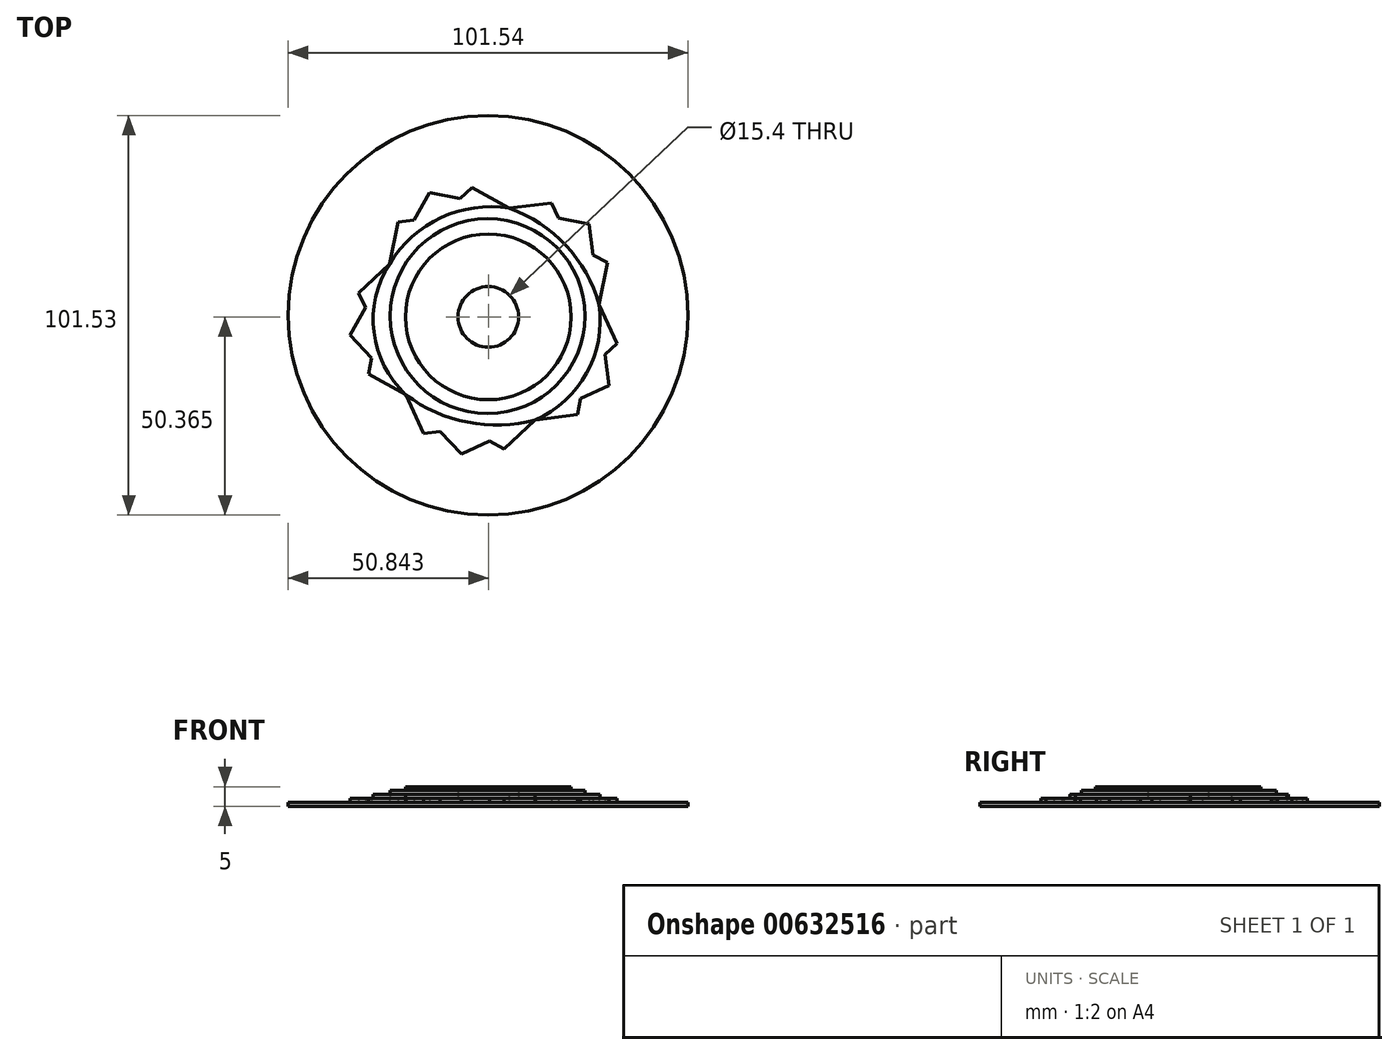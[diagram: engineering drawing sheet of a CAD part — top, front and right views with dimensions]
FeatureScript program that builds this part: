
annotation { "Feature Type Name" : "Feature", "Feature Type Description" : "" }
export const myFeature = defineFeature(function(context is Context, id is Id, definition is map)
    precondition{}
    {
        {
            var Q0;
            Q0=qCreatedBy(makeId("Top.planeOp"),FACE);
            var sketch = newSketch(context, id + "F0", { "sketchPlane" : qUnion([Q0])});
            skCircle(sketch, "E0.cCircle", {"center": v(-32.14, 16.2) * mm, "radius": 27.07 * mm, "construction": true});
            skLineSegment(sketch, "E0.0", {"start": v(0.71, 9.84) * mm, "end": v(-28.04, -17) * mm});
            skLineSegment(sketch, "E0.1", {"start": v(-28.04, -17) * mm, "end": v(-62.46, 2.05) * mm});
            skLineSegment(sketch, "E0.2", {"start": v(-62.46, 2.05) * mm, "end": v(-54.97, 40.67) * mm});
            skLineSegment(sketch, "E0.3", {"start": v(-54.97, 40.67) * mm, "end": v(-15.93, 45.48) * mm});
            skLineSegment(sketch, "E0.4", {"start": v(-15.93, 45.48) * mm, "end": v(0.71, 9.84) * mm});
            skPoint(sketch, "E0.0.midPoint", {"position": v(-13.66, -3.58) * mm});
            skLineSegment(sketch, "E1.0", {"start": v(-1.78, 30.3) * mm, "end": v(-9.36, -8.3) * mm});
            skLineSegment(sketch, "E1.1", {"start": v(-9.36, -8.3) * mm, "end": v(-48.4, -13.03) * mm});
            skLineSegment(sketch, "E1.2", {"start": v(-48.4, -13.03) * mm, "end": v(-64.97, 22.65) * mm});
            skLineSegment(sketch, "E1.3", {"start": v(-64.97, 22.65) * mm, "end": v(-36.16, 49.43) * mm});
            skLineSegment(sketch, "E1.4", {"start": v(-36.16, 49.43) * mm, "end": v(-1.78, 30.3) * mm});
            skPoint(sketch, "E1.0.midPoint", {"position": v(-5.57, 11) * mm});
            skCircle(sketch, "E2.cCircle", {"center": v(-32.14, 16.2) * mm, "radius": 28.47 * mm, "construction": true});
            skLineSegment(sketch, "E2.0", {"start": v(-6.38, 40.2) * mm, "end": v(-1.36, -0.87) * mm});
            skLineSegment(sketch, "E2.1", {"start": v(-1.36, -0.87) * mm, "end": v(-38.87, -18.34) * mm});
            skLineSegment(sketch, "E2.2", {"start": v(-38.87, -18.34) * mm, "end": v(-67.07, 11.94) * mm});
            skLineSegment(sketch, "E2.3", {"start": v(-67.07, 11.94) * mm, "end": v(-47, 48.12) * mm});
            skLineSegment(sketch, "E2.4", {"start": v(-47, 48.12) * mm, "end": v(-6.38, 40.2) * mm});
            skPoint(sketch, "E2.0.midPoint", {"position": v(-3.87, 19.66) * mm});
            skCircle(sketch, "E3", {"center": v(-32.14, 16.2) * mm, "radius": 9.35 * mm});
            skSolve(sketch);
        }
        {
            var Q0;
            Q0 = qSketchRegion(id + "F0", true);
            extrude(context, id + "F1", {"entities" : qUnion([Q0]), "depth" : 2 * mm, "offsetDistance" : 25.4 * mm});
        }
        {
            var Q0;
            Q0=qCreatedBy(makeId("Top.planeOp"),FACE);
            var sketch = newSketch(context, id + "F2", { "sketchPlane" : qUnion([Q0])});
            skArc(sketch, "E4", {"start": v(-26.7, 44.14) * mm, "mid": v(-44.02, 41.77) * mm, "end": v(-57, 30.04) * mm});
            skArc(sketch, "E5", {"start": v(-3.92, 19.67) * mm, "mid": v(-12.27, 34.73) * mm, "end": v(-26.7, 44.14) * mm});
            skArc(sketch, "E6", {"start": v(-20.1, -9.62) * mm, "mid": v(-7.03, 2.28) * mm, "end": v(-3.92, 19.67) * mm});
            skArc(sketch, "E7", {"start": v(-52.97, -3.23) * mm, "mid": v(-37.27, -10.21) * mm, "end": v(-20.1, -9.62) * mm});
            skArc(sketch, "E8", {"start": v(-57, 30.04) * mm, "mid": v(-61.07, 12.67) * mm, "end": v(-52.97, -3.23) * mm});
            skCircle(sketch, "E9", {"center": v(-31.44, 17.25) * mm, "radius": 9.93 * mm});
            skSolve(sketch);
        }
        {
            var Q0;
            Q0 = qSketchRegion(id + "F2", true);
            extrude(context, id + "F3", {"entities" : qUnion([Q0]), "operationType" : NewBodyOperationType.ADD, "depth" : 3 * mm, "offsetDistance" : 25 * mm});
        }
        {
            var Q0;
            Q0=qCreatedBy(makeId("Top.planeOp"),FACE);
            var sketch = newSketch(context, id + "F4", { "sketchPlane" : qUnion([Q0])});
            skCircle(sketch, "E10", {"center": v(-32.2, 16.74) * mm, "radius": 24.75 * mm});
            skCircle(sketch, "E11", {"center": v(-32.2, 16.74) * mm, "radius": 9.98 * mm});
            skSolve(sketch);
        }
        {
            var Q0;
            Q0 = qSketchRegion(id + "F4", true);
            extrude(context, id + "F5", {"entities" : qUnion([Q0]), "operationType" : NewBodyOperationType.ADD, "depth" : 4 * mm, "offsetDistance" : 25 * mm});
        }
        {
            var Q0;
            Q0=qCreatedBy(makeId("Top.planeOp"),FACE);
            var sketch = newSketch(context, id + "F6", { "sketchPlane" : qUnion([Q0])});
            skCircle(sketch, "E12", {"center": v(-32, 16.56) * mm, "radius": 21.05 * mm});
            skCircle(sketch, "E13", {"center": v(-32, 16.56) * mm, "radius": 7.7 * mm});
            skSolve(sketch);
        }
        {
            var Q0;
            Q0 = qSketchRegion(id + "F6", true);
            extrude(context, id + "F7", {"entities" : qUnion([Q0]), "operationType" : NewBodyOperationType.ADD, "depth" : 5 * mm, "offsetDistance" : 25 * mm});
        }
        {
            var Q0;
            Q0=qCreatedBy(makeId("Top.planeOp"),FACE);
            var sketch = newSketch(context, id + "F8", { "sketchPlane" : qUnion([Q0])});
            skCircle(sketch, "E14", {"center": v(-32.08, 16.96) * mm, "radius": 50.77 * mm});
            skCircle(sketch, "E15", {"center": v(-32.08, 16.96) * mm, "radius": 10.13 * mm});
            skSolve(sketch);
        }
        {
            var Q0;
            Q0 = qSketchRegion(id + "F8", true);
            extrude(context, id + "F9", {"entities" : qUnion([Q0]), "operationType" : NewBodyOperationType.ADD, "depth" : 1 * mm, "offsetDistance" : 25 * mm});
        }
    });
